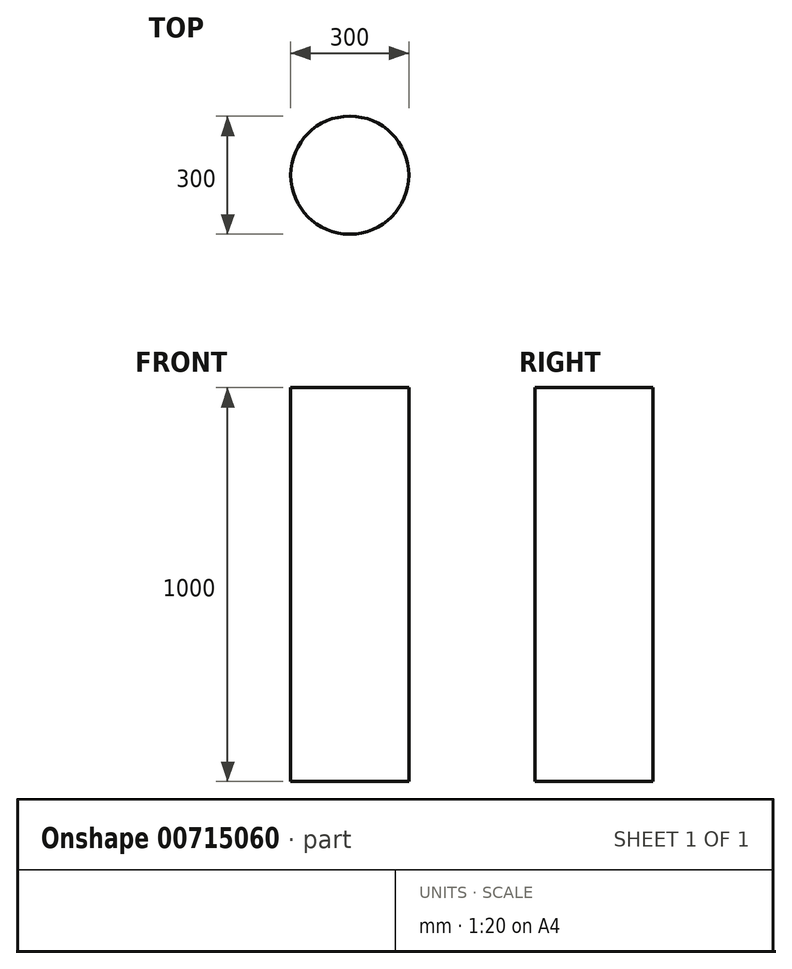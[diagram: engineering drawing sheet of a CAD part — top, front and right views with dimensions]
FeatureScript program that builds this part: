
annotation { "Feature Type Name" : "Feature", "Feature Type Description" : "" }
export const myFeature = defineFeature(function(context is Context, id is Id, definition is map)
    precondition{}
    {
        {
            var Q0;
            Q0=qCreatedBy(makeId("Top.planeOp"),FACE);
            var sketch = newSketch(context, id + "F0", { "sketchPlane" : qUnion([Q0])});
            skCircle(sketch, "E0", {"center": v(0, 0) * mm, "radius": 150 * mm});
            skSolve(sketch);
        }
        {
            var Q0;
            Q0=makeQuery(id+"F0.imprint","IMPRINT",FACE,{"disambiguationData":[TD([[makeQuery(id+"F0.imprint","IMPRINT",EDGE,{"derivedFrom":sQuery(id+"F0.wireOp",EDGE,"E0")}),1.0]])]});
            extrude(context, id + "F1", {"entities" : qUnion([Q0]), "oppositeDirection" : true, "depth" : 1000 * mm, "offsetDistance" : 25 * mm});
        }
    });
